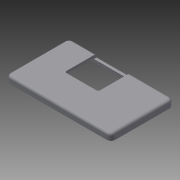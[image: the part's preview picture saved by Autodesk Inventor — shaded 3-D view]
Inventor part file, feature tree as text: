
AUTODESK INVENTOR PART (.ipt)
format: ipt  version: 2013 (Build 170138000, 138)  size: 150,016 bytes
history: native  units: in
note: dims shown in document units (in); Inventor stores cm internally (conversion verified against a paired STEP export)
features: extrude x3, sketch x3, fillet x2
ambient origin geometry x8: Origin, YZ Plane, XZ Plane, XY Plane, X Axis, Y Axis, Z Axis, Center Point
bodies: Solid1 (feature_tree)
feature tree (8):
  extrude  "Extrusion1"  Depth=2.9528in
  fillet  "Fillet1"  Radius=0.1969in
  extrude  "Extrusion2"  Depth=0.1181in
  fillet  "Fillet2"  Radius=0.3937in
  extrude  "Extrusion3"  Depth=0.1969in TaperAngle=0.0deg
  sketch  "Sketch1"  dims[d0=4.9213in d4=2.9528in d5=0.1969in]
  sketch  "Sketch2"  dims[d6=0.315in d7=0.0in d8=0.1181in d9=0.3937in]
  sketch  "Sketch3"  dims[d10=0.1181in d11=0.1969in d12=0.0in d13=0.0787in d14=1.5748in d15=1.5748in d16=0.0787in d17=0.1969in d18=0.1575in d19=0.0in d21=2.0787in]
